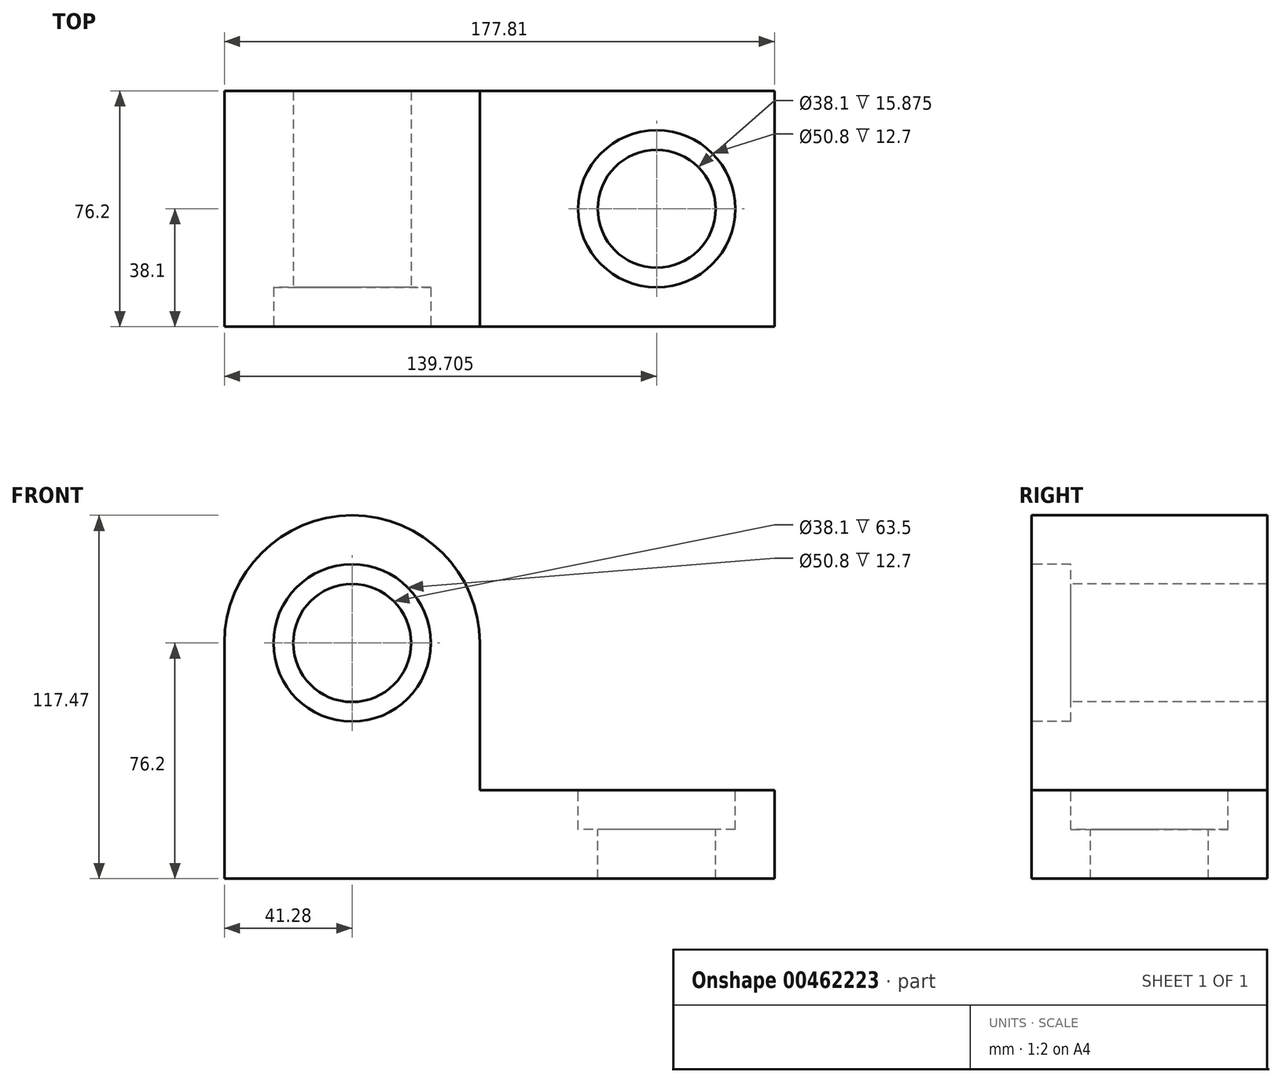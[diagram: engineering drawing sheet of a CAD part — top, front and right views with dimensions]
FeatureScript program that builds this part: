
annotation { "Feature Type Name" : "Feature", "Feature Type Description" : "" }
export const myFeature = defineFeature(function(context is Context, id is Id, definition is map)
    precondition{}
    {
        {
            var Q0;
            Q0=qCreatedBy(makeId("Front.planeOp"),FACE);
            var sketch = newSketch(context, id + "F0", { "sketchPlane" : qUnion([Q0])});
            skLineSegment(sketch, "E0", {"start": v(-41.28, 0) * mm, "end": v(-41.27, -76.2) * mm});
            skLineSegment(sketch, "E1", {"start": v(-41.28, -76.2) * mm, "end": v(136.53, -76.2) * mm});
            skLineSegment(sketch, "E2", {"start": v(136.53, -76.2) * mm, "end": v(136.53, -47.62) * mm});
            skLineSegment(sketch, "E3", {"start": v(136.53, -47.62) * mm, "end": v(41.28, -47.62) * mm});
            skLineSegment(sketch, "E4", {"start": v(41.28, -47.63) * mm, "end": v(41.28, 0) * mm});
            skArc(sketch, "E5", {"start": v(41.28, 0) * mm, "mid": v(0, 41.28) * mm, "end": v(-41.28, 0) * mm});
            skSolve(sketch);
        }
        {
            var Q0;
            Q0=makeQuery(id+"F0.imprint","IMPRINT",FACE,{"disambiguationData":[TD([[makeQuery(id+"F0.imprint","IMPRINT",EDGE,{"derivedFrom":sQuery(id+"F0.wireOp",EDGE,"E0")}),1.0]])]});
            extrude(context, id + "F1", {"entities" : qUnion([Q0]), "depth" : 76.2 * mm, "symmetric" : true});
        }
        {
            var Q0;
            Q0=makeQuery(id+"F1.opExtrude","CAP_FACE",FACE,{"disambiguationData":[OSD([sQuery(id+"F0.wireOp",EDGE,"E0"),sQuery(id+"F0.wireOp",EDGE,"E1"),sQuery(id+"F0.wireOp",EDGE,"E2"),sQuery(id+"F0.wireOp",EDGE,"E3"),sQuery(id+"F0.wireOp",EDGE,"E4"),sQuery(id+"F0.wireOp",EDGE,"E5")])],"isStart":false});
            var sketch = newSketch(context, id + "F2", { "sketchPlane" : qUnion([Q0])});
            skPoint(sketch, "E6", {"position": v(0, 0) * mm});
            skSolve(sketch);
        }
        {
            var Q0;
            Q0=sQuery(id+"F2.wireOp",VERTEX,"E6");
            var Q1;
            Q1=makeQuery(id+"F1.opExtrude","SWEPT_BODY",BODY,{"disambiguationData":[OSD([sQuery(id+"F0.wireOp",EDGE,"E0"),sQuery(id+"F0.wireOp",EDGE,"E1"),sQuery(id+"F0.wireOp",EDGE,"E2"),sQuery(id+"F0.wireOp",EDGE,"E3"),sQuery(id+"F0.wireOp",EDGE,"E4"),sQuery(id+"F0.wireOp",EDGE,"E5")])]});
            hole(context, id + "F3", {"style" : HoleStyle.C_BORE, "endStyle" : HoleEndStyle.THROUGH, "holeDiameter" : 38.1 * mm, "cBoreDiameter" : 50.8 * mm, "cBoreDepth" : 12.7 * mm, "isTappedThrough" : true, "tappedDepth" : 12.7 * mm, "tapClearance" : 3, "locations" : qUnion([Q0]), "scope" : qUnion([Q1])});
        }
        {
            var Q0;
            Q0=makeQuery(id+"F1.opExtrude","SWEPT_FACE",FACE,{"disambiguationData":[OSD([sQuery(id+"F0.wireOp",EDGE,"E3")])]});
            var sketch = newSketch(context, id + "F4", { "sketchPlane" : qUnion([Q0])});
            skPoint(sketch, "E7", {"position": v(98.43, 0) * mm});
            skSolve(sketch);
        }
        {
            var Q0;
            Q0=sQuery(id+"F4.wireOp",VERTEX,"E7");
            var Q1;
            Q1=makeQuery(id+"F1.opExtrude","SWEPT_BODY",BODY,{"disambiguationData":[OSD([sQuery(id+"F0.wireOp",EDGE,"E0"),sQuery(id+"F0.wireOp",EDGE,"E1"),sQuery(id+"F0.wireOp",EDGE,"E2"),sQuery(id+"F0.wireOp",EDGE,"E3"),sQuery(id+"F0.wireOp",EDGE,"E4"),sQuery(id+"F0.wireOp",EDGE,"E5")])]});
            hole(context, id + "F5", {"style" : HoleStyle.C_BORE, "endStyle" : HoleEndStyle.THROUGH, "holeDiameter" : 38.1 * mm, "cBoreDiameter" : 50.8 * mm, "cBoreDepth" : 12.7 * mm, "isTappedThrough" : true, "tappedDepth" : 12.7 * mm, "tapClearance" : 3, "locations" : qUnion([Q0]), "scope" : qUnion([Q1])});
        }
    });
